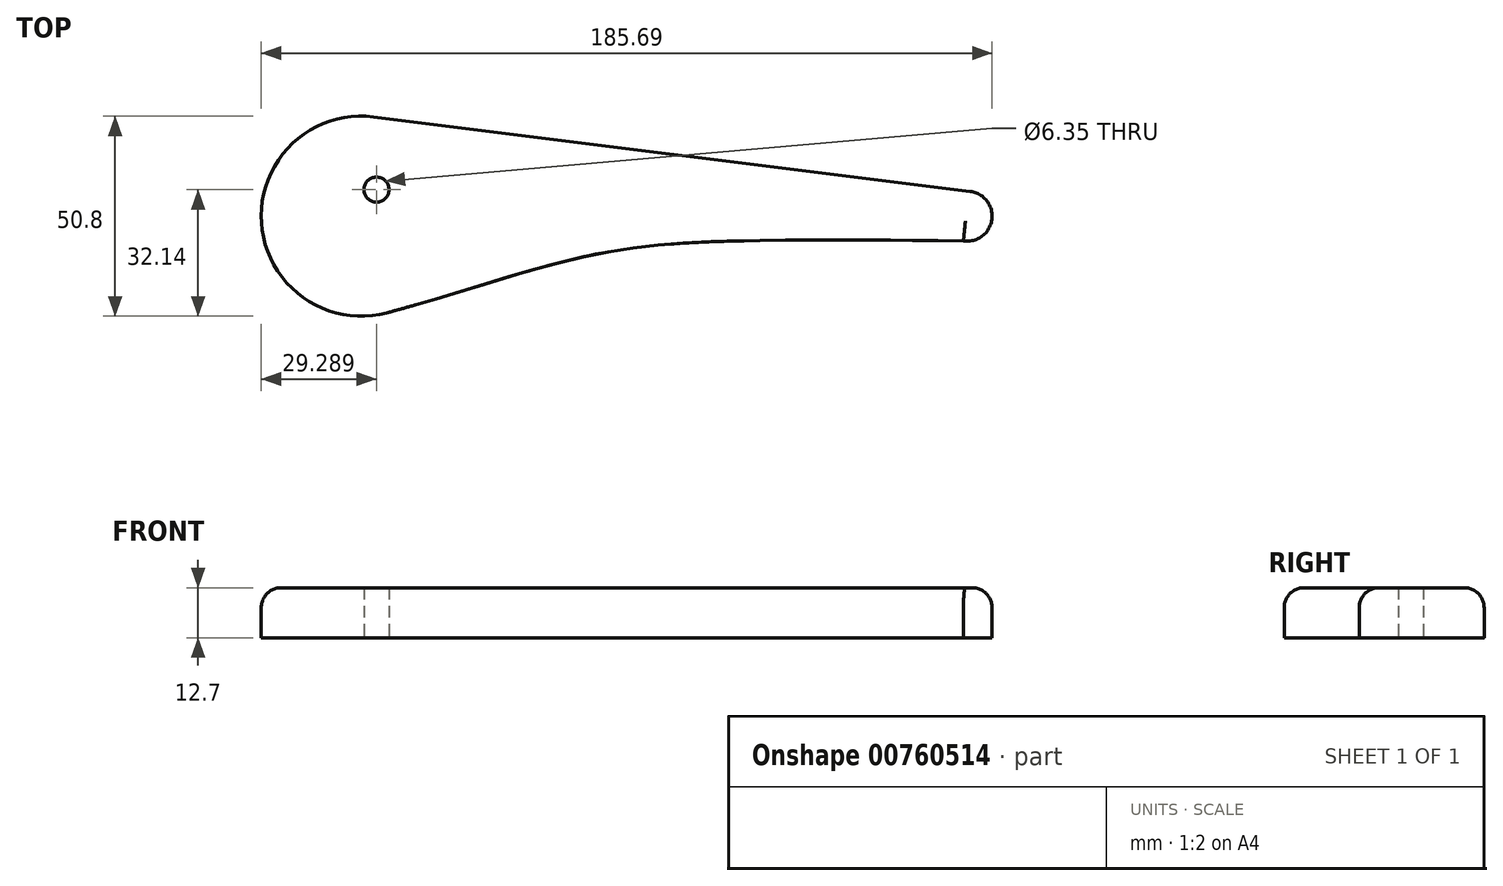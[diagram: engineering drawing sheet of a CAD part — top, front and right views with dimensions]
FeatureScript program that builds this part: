
annotation { "Feature Type Name" : "Feature", "Feature Type Description" : "" }
export const myFeature = defineFeature(function(context is Context, id is Id, definition is map)
    precondition{}
    {
        {
            var Q0;
            Q0=qCreatedBy(makeId("Top.planeOp"),FACE);
            var sketch = newSketch(context, id + "F0", { "sketchPlane" : qUnion([Q0])});
            skCircle(sketch, "E0", {"center": v(-77.6, 0) * mm, "radius": 25.4 * mm});
            skCircle(sketch, "E1", {"center": v(76.34, 0) * mm, "radius": 6.35 * mm});
            skLineSegment(sketch, "E2", {"start": v(-74.46, 25.2) * mm, "end": v(77.12, 6.3) * mm});
            skFitSpline(sketch, "E3", {"points": [v(-71.08, -24.55) * mm, v(-20.66, -10.22) * mm, v(17.61, -6.3) * mm, v(77.11, -6.3) * mm], "startDerivative": vector(160.76, 42.68) * mm, "endDerivative": vector(175.06, -1.9) * mm});
            skCircle(sketch, "E4", {"center": v(-73.71, 6.74) * mm, "radius": 3.18 * mm});
            skSolve(sketch);
        }
        {
            var Q0;
            Q0 = qSketchRegion(id + "F0", true);
            extrude(context, id + "F1", {"entities" : qUnion([Q0]), "depth" : 12.7 * mm, "offsetDistance" : 25.4 * mm});
        }
        {
            var Q0;
            Q0=makeQuery(id+"F1.opExtrude","CAP_EDGE",EDGE,{"disambiguationData":[OSD([sQuery(id+"F0.wireOp",EDGE,"E0")])],"isStart":false});
            var Q1;
            Q1=makeQuery(id+"F1.opExtrude","CAP_EDGE",EDGE,{"disambiguationData":[OSD([sQuery(id+"F0.wireOp",EDGE,"E3")])],"isStart":false});
            var Q2;
            Q2=makeQuery(id+"F1.opExtrude","CAP_EDGE",EDGE,{"disambiguationData":[OSD([sQuery(id+"F0.wireOp",EDGE,"E2")])],"isStart":false});
            var Q3;
            Q3=makeQuery(id+"F1.opExtrude","CAP_EDGE",EDGE,{"disambiguationData":[OSD([sQuery(id+"F0.wireOp",EDGE,"E1")])],"isStart":false});
            fillet(context, id + "F2", {"entities" : qUnion([Q0, Q1, Q2, Q3]), "radius" : 5.08 * mm, "tangentPropagation" : true, "allowEdgeOverflow" : false});
        }
    });
